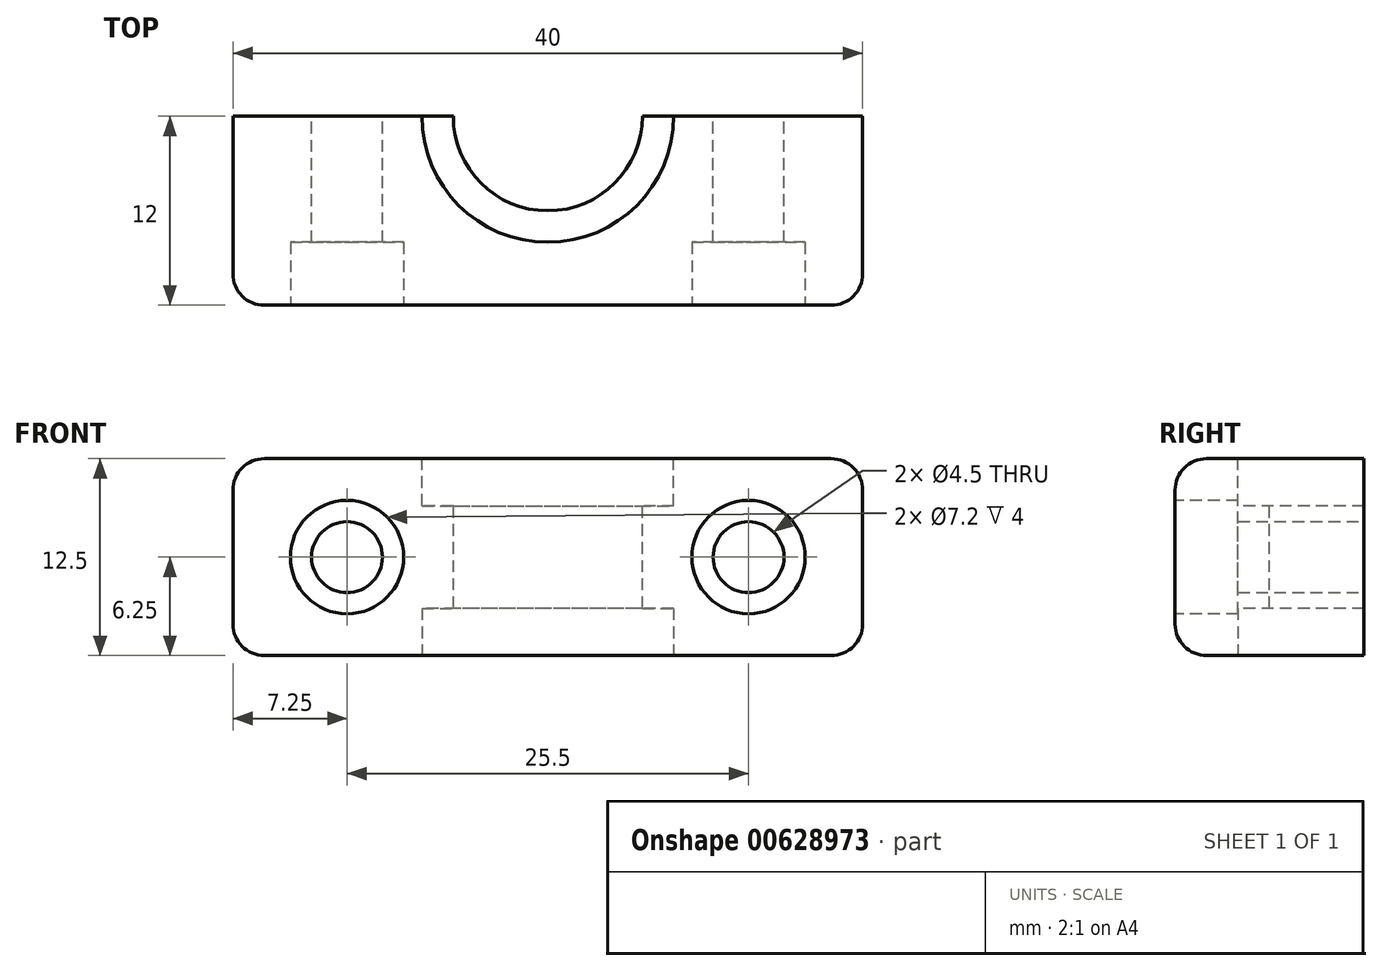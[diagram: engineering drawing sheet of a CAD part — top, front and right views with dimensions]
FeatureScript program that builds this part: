
annotation { "Feature Type Name" : "Feature", "Feature Type Description" : "" }
export const myFeature = defineFeature(function(context is Context, id is Id, definition is map)
    precondition{}
    {
        {
            var Q0;
            Q0=qCreatedBy(makeId("Front.planeOp"),FACE);
            var sketch = newSketch(context, id + "F0", { "sketchPlane" : qUnion([Q0])});
            skLineSegment(sketch, "E0.bottom", {"start": v(20, 6.25) * mm, "end": v(-20, 6.25) * mm});
            skLineSegment(sketch, "E0.top", {"start": v(20, -6.25) * mm, "end": v(-20, -6.25) * mm});
            skLineSegment(sketch, "E0.left", {"start": v(20, 6.25) * mm, "end": v(20, -6.25) * mm});
            skLineSegment(sketch, "E0.right", {"start": v(-20, 6.25) * mm, "end": v(-20, -6.25) * mm});
            skPoint(sketch, "E0.middle", {"position": v(0, 0) * mm});
            skCircle(sketch, "E1", {"center": v(-12.75, 0) * mm, "radius": 2.25 * mm});
            skCircle(sketch, "E2", {"center": v(12.75, 0) * mm, "radius": 2.25 * mm});
            skSolve(sketch);
        }
        {
            var Q0;
            Q0=makeQuery(id+"F0.imprint","IMPRINT",FACE,{"disambiguationData":[TD([[makeQuery(id+"F0.imprint","IMPRINT",EDGE,{"derivedFrom":sQuery(id+"F0.wireOp",EDGE,"E0.bottom")}),1.0]])]});
            extrude(context, id + "F1", {"entities" : qUnion([Q0]), "depth" : 6 * mm, "offsetDistance" : 25 * mm, "hasSecondDirection" : true, "secondDirectionOppositeDirection" : true, "secondDirectionDepth" : 6 * mm});
        }
        {
            var Q0;
            Q0=makeQuery(id+"F1.opExtrude","CAP_FACE",FACE,{"disambiguationData":[OSD([sQuery(id+"F0.wireOp",EDGE,"E0.bottom"),sQuery(id+"F0.wireOp",EDGE,"E0.top"),sQuery(id+"F0.wireOp",EDGE,"E0.left"),sQuery(id+"F0.wireOp",EDGE,"E0.right"),sQuery(id+"F0.wireOp",EDGE,"E1"),sQuery(id+"F0.wireOp",EDGE,"E2")])],"isStart":false});
            var sketch = newSketch(context, id + "F2", { "sketchPlane" : qUnion([Q0])});
            skCircle(sketch, "E3", {"center": v(-12.75, 0) * mm, "radius": 3.6 * mm});
            skCircle(sketch, "E4", {"center": v(12.75, 0) * mm, "radius": 3.6 * mm});
            skSolve(sketch);
        }
        {
            var Q0;
            Q0 = qSketchRegion(id + "F2", true);
            extrude(context, id + "F3", {"entities" : qUnion([Q0]), "operationType" : NewBodyOperationType.REMOVE, "oppositeDirection" : true, "depth" : 4 * mm, "offsetDistance" : 25 * mm});
        }
        {
            var Q0;
            Q0=makeQuery(id+"F1.opExtrude","SWEPT_EDGE",EDGE,{"disambiguationData":[OSD([sQuery(id+"F0.wireOp",EDGE,"E0.bottom"),sQuery(id+"F0.wireOp",EDGE,"E0.right")])]});
            var Q1;
            Q1=makeQuery(id+"F1.opExtrude","SWEPT_EDGE",EDGE,{"disambiguationData":[OSD([sQuery(id+"F0.wireOp",EDGE,"E0.top"),sQuery(id+"F0.wireOp",EDGE,"E0.right")])]});
            var Q2;
            Q2=makeQuery(id+"F1.opExtrude","SWEPT_EDGE",EDGE,{"disambiguationData":[OSD([sQuery(id+"F0.wireOp",EDGE,"E0.bottom"),sQuery(id+"F0.wireOp",EDGE,"E0.left")])]});
            var Q3;
            Q3=makeQuery(id+"F1.opExtrude","SWEPT_EDGE",EDGE,{"disambiguationData":[OSD([sQuery(id+"F0.wireOp",EDGE,"E0.top"),sQuery(id+"F0.wireOp",EDGE,"E0.left")])]});
            var Q4;
            Q4=makeQuery(id+"F1.opExtrude","CAP_EDGE",EDGE,{"disambiguationData":[OSD([sQuery(id+"F0.wireOp",EDGE,"E0.left")])],"isStart":false});
            var Q5;
            Q5=makeQuery(id+"F1.opExtrude","CAP_EDGE",EDGE,{"disambiguationData":[OSD([sQuery(id+"F0.wireOp",EDGE,"E0.bottom")])],"isStart":false});
            var Q6;
            Q6=makeQuery(id+"F1.opExtrude","CAP_EDGE",EDGE,{"disambiguationData":[OSD([sQuery(id+"F0.wireOp",EDGE,"E0.top")])],"isStart":false});
            var Q7;
            Q7=makeQuery(id+"F1.opExtrude","CAP_EDGE",EDGE,{"disambiguationData":[OSD([sQuery(id+"F0.wireOp",EDGE,"E0.right")])],"isStart":false});
            fillet(context, id + "F4", {"entities" : qUnion([Q0, Q1, Q2, Q3, Q4, Q5, Q6, Q7]), "radius" : 2 * mm, "tangentPropagation" : true, "allowEdgeOverflow" : false});
        }
        {
            var Q0;
            Q0=qCreatedBy(makeId("Top.planeOp"),FACE);
            var sketch = newSketch(context, id + "F5", { "sketchPlane" : qUnion([Q0])});
            skArc(sketch, "E5", {"start": v(-6, 6) * mm, "mid": v(0, 0) * mm, "end": v(6, 6) * mm});
            skLineSegment(sketch, "E6", {"start": v(-6, 6) * mm, "end": v(6, 6) * mm});
            skSolve(sketch);
        }
        {
            var Q0;
            Q0 = qSketchRegion(id + "F5", true);
            extrude(context, id + "F6", {"entities" : qUnion([Q0]), "operationType" : NewBodyOperationType.REMOVE, "endBound" : BoundingType.UP_TO_NEXT, "oppositeDirection" : true, "depth" : 25 * mm, "offsetDistance" : 25 * mm, "hasSecondDirection" : true, "secondDirectionBound" : SecondDirectionBoundingType.UP_TO_NEXT, "secondDirectionOppositeDirection" : false, "secondDirectionDepth" : 25 * mm});
        }
        {
            var Q0;
            Q0=makeQuery(id+"F1.opExtrude","SWEPT_FACE",FACE,{"disambiguationData":[OSD([sQuery(id+"F0.wireOp",EDGE,"E0.bottom")])]});
            var sketch = newSketch(context, id + "F7", { "sketchPlane" : qUnion([Q0])});
            skCircle(sketch, "E7", {"center": v(0, 6) * mm, "radius": 8 * mm});
            skSolve(sketch);
        }
        {
            var Q0;
            Q0 = qSketchRegion(id + "F7", true);
            extrude(context, id + "F8", {"entities" : qUnion([Q0]), "operationType" : NewBodyOperationType.REMOVE, "oppositeDirection" : true, "depth" : 3 * mm, "offsetDistance" : 25 * mm});
        }
        {
            var Q0;
            Q0=makeQuery(id+"F1.opExtrude","SWEPT_FACE",FACE,{"disambiguationData":[OSD([sQuery(id+"F0.wireOp",EDGE,"E0.top")])]});
            var sketch = newSketch(context, id + "F9", { "sketchPlane" : qUnion([Q0])});
            skCircle(sketch, "E8", {"center": v(0, -6) * mm, "radius": 8 * mm});
            skSolve(sketch);
        }
        {
            var Q0;
            Q0 = qSketchRegion(id + "F9", true);
            extrude(context, id + "F10", {"entities" : qUnion([Q0]), "operationType" : NewBodyOperationType.REMOVE, "oppositeDirection" : true, "depth" : 3 * mm, "offsetDistance" : 25 * mm});
        }
    });
